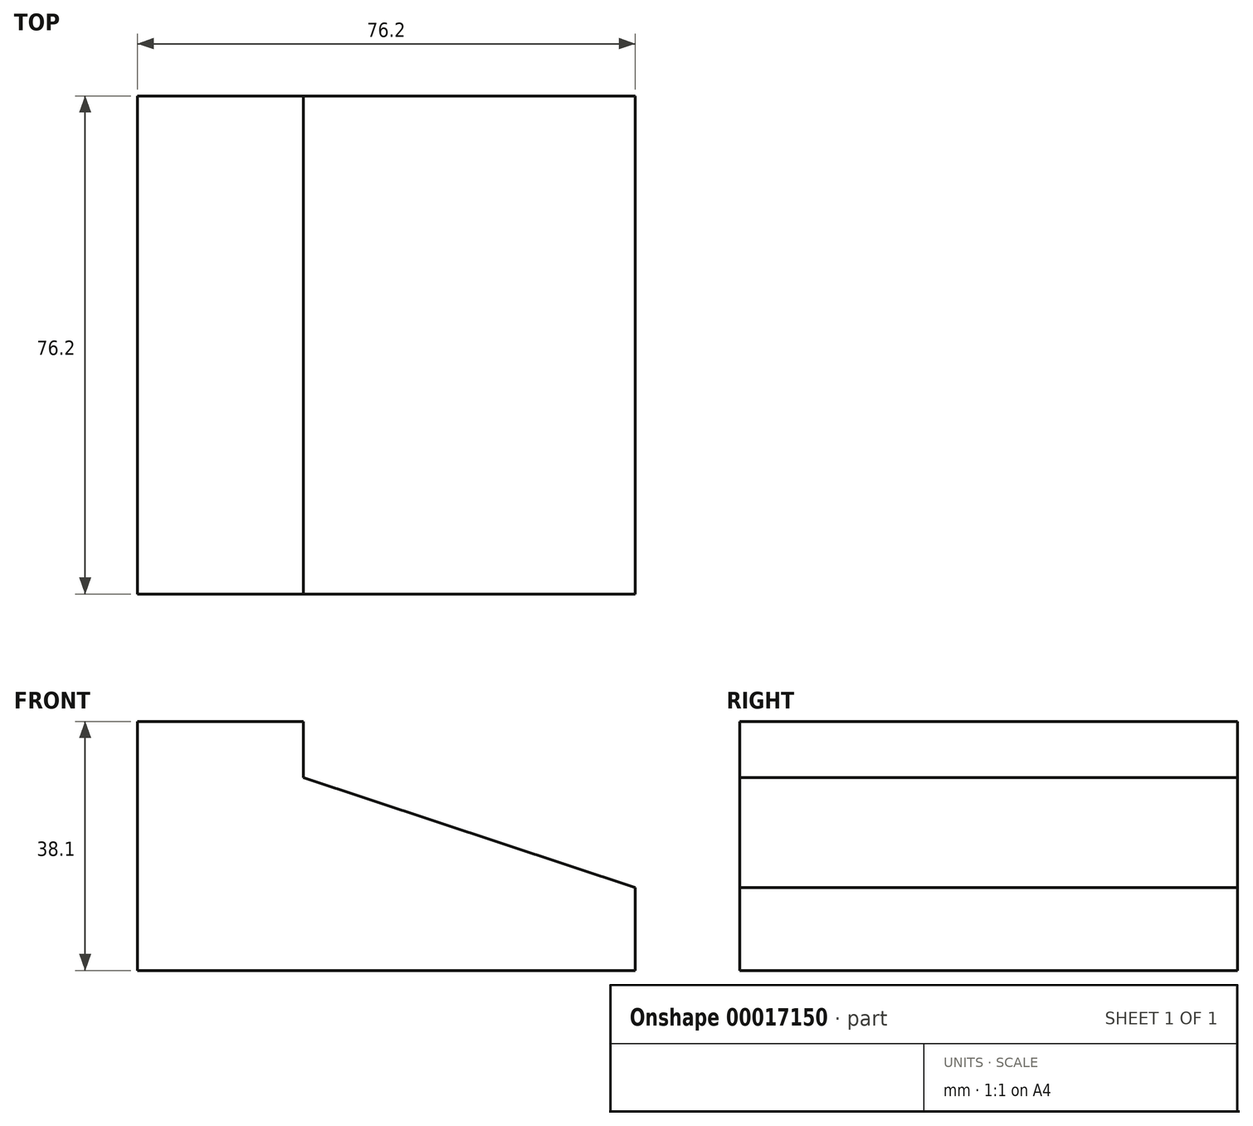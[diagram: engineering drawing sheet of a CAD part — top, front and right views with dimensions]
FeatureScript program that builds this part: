
annotation { "Feature Type Name" : "Feature", "Feature Type Description" : "" }
export const myFeature = defineFeature(function(context is Context, id is Id, definition is map)
    precondition{}
    {
        {
            var Q0;
            Q0=qCreatedBy(makeId("Front.planeOp"),FACE);
            var sketch = newSketch(context, id + "F0", { "sketchPlane" : qUnion([Q0])});
            skLineSegment(sketch, "E0", {"start": v(32.44, 2.06) * mm, "end": v(32.44, -10.64) * mm});
            skLineSegment(sketch, "E1", {"start": v(32.44, -10.64) * mm, "end": v(-43.76, -10.64) * mm});
            skLineSegment(sketch, "E2", {"start": v(-43.76, -10.64) * mm, "end": v(-43.76, 27.46) * mm});
            skLineSegment(sketch, "E3", {"start": v(-43.76, 27.46) * mm, "end": v(-18.36, 27.46) * mm});
            skLineSegment(sketch, "E4", {"start": v(-18.36, 27.46) * mm, "end": v(-18.36, 18.85) * mm});
            skLineSegment(sketch, "E5", {"start": v(-18.36, 18.85) * mm, "end": v(32.44, 2.06) * mm});
            skSolve(sketch);
        }
        {
            var Q0;
            Q0 = qSketchRegion(id + "F0", true);
            extrude(context, id + "F1", {"entities" : qUnion([Q0]), "depth" : 76.2 * mm});
        }
    });
